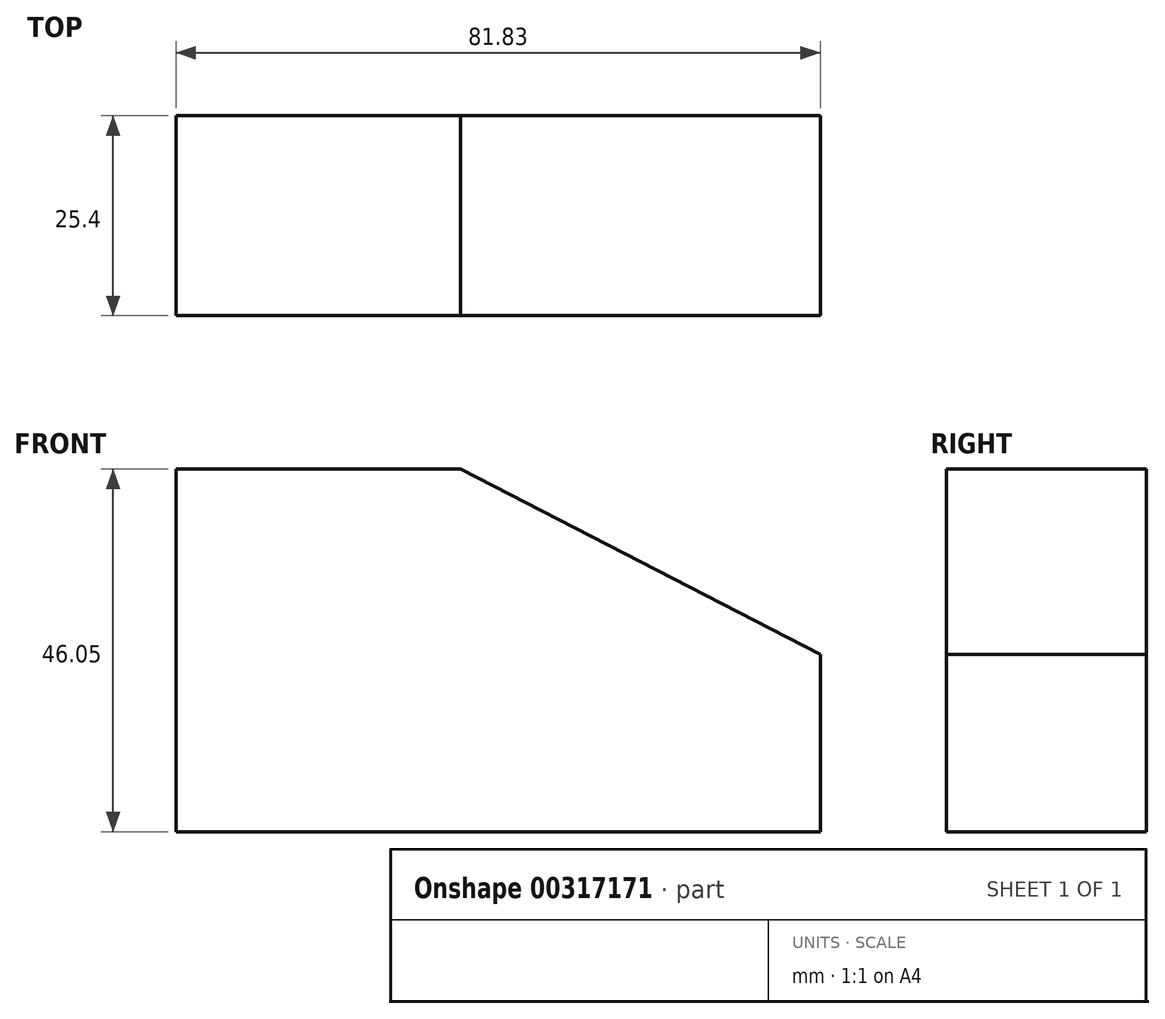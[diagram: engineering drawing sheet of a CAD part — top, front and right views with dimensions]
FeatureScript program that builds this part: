
annotation { "Feature Type Name" : "Feature", "Feature Type Description" : "" }
export const myFeature = defineFeature(function(context is Context, id is Id, definition is map)
    precondition{}
    {
        {
            var Q0;
            Q0=qCreatedBy(makeId("Front.planeOp"),FACE);
            var sketch = newSketch(context, id + "F0", { "sketchPlane" : qUnion([Q0])});
            skLineSegment(sketch, "E0", {"start": v(-41.25, -46.05) * mm, "end": v(-41.25, 0) * mm});
            skLineSegment(sketch, "E1", {"start": v(-41.25, 0) * mm, "end": v(-5.14, 0) * mm});
            skLineSegment(sketch, "E2", {"start": v(-41.25, -46.05) * mm, "end": v(40.58, -46.05) * mm});
            skLineSegment(sketch, "E3", {"start": v(40.58, -46.05) * mm, "end": v(40.58, -23.52) * mm});
            skLineSegment(sketch, "E4", {"start": v(40.58, -23.52) * mm, "end": v(-5.14, 0) * mm});
            skSolve(sketch);
        }
        {
            var Q0;
            Q0=makeQuery(id+"F0.imprint","IMPRINT",FACE,{"disambiguationData":[TD([[makeQuery(id+"F0.imprint","IMPRINT",EDGE,{"derivedFrom":sQuery(id+"F0.wireOp",EDGE,"E0")}),-1.0]])]});
            extrude(context, id + "F1", {"entities" : qUnion([Q0]), "depth" : 25.4 * mm});
        }
    });
